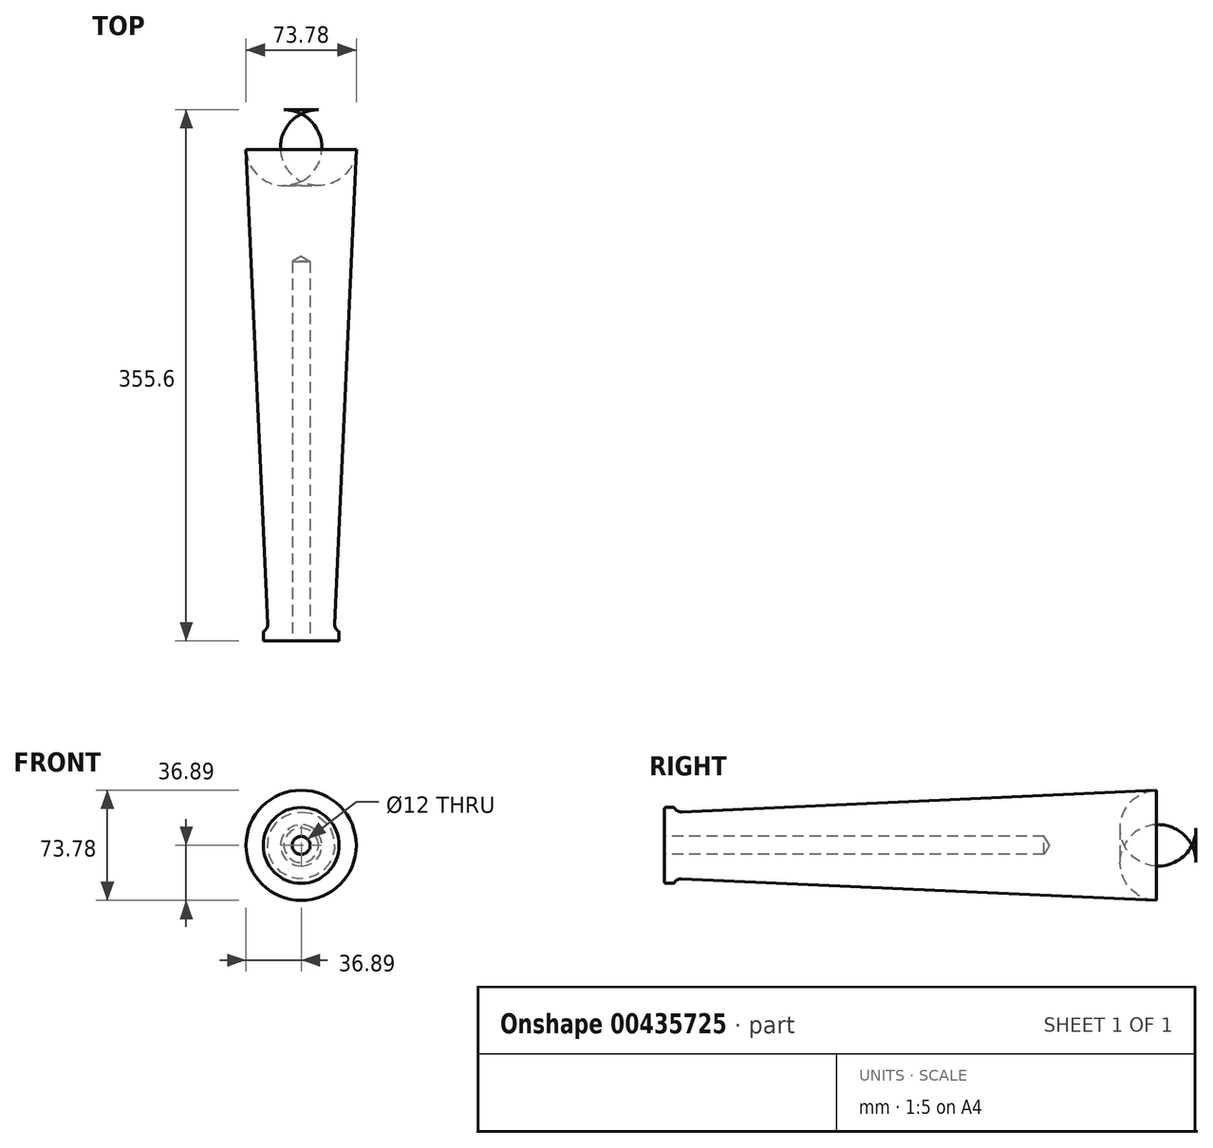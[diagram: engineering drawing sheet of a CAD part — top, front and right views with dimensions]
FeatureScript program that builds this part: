
annotation { "Feature Type Name" : "Feature", "Feature Type Description" : "" }
export const myFeature = defineFeature(function(context is Context, id is Id, definition is map)
    precondition{}
    {
        {
            var Q0;
            Q0=qCreatedBy(makeId("Right.planeOp"),FACE);
            var sketch = newSketch(context, id + "F0", { "sketchPlane" : qUnion([Q0])});
            skLineSegment(sketch, "E0", {"start": v(-254, 25.4) * mm, "end": v(-247.65, 25.4) * mm});
            skLineSegment(sketch, "E1", {"start": v(-247.65, 25.4) * mm, "end": v(-247.65, 22.22) * mm});
            skLineSegment(sketch, "E2", {"start": v(-247.65, 22.22) * mm, "end": v(101.6, 38.1) * mm});
            skLineSegment(sketch, "E3", {"start": v(101.6, 38.1) * mm, "end": v(101.6, 0) * mm});
            skLineSegment(sketch, "E4", {"start": v(-254, 25.4) * mm, "end": v(-254, 0) * mm});
            skLineSegment(sketch, "E5", {"start": v(-254, 0) * mm, "end": v(101.6, 0) * mm});
            skSolve(sketch);
        }
        {
            var Q0;
            Q0=makeQuery(id+"F0.imprint","IMPRINT",FACE,{"disambiguationData":[TD([[makeQuery(id+"F0.imprint","IMPRINT",EDGE,{"derivedFrom":sQuery(id+"F0.wireOp",EDGE,"E0")}),-1.0]])]});
            var Q1;
            Q1=sQuery(id+"F0.wireOp",EDGE,"E5");
            revolve(context, id + "F1", {"entities" : qUnion([Q0]), "axis" : qUnion([Q1]), "revolveType" : RevolveType.FULL});
        }
        {
            var Q0;
            Q0=makeQuery(id+"F1.opRevolve","SWEPT_EDGE",EDGE,{"disambiguationData":[OSD([sQuery(id+"F0.wireOp",EDGE,"E1"),sQuery(id+"F0.wireOp",EDGE,"E2")])]});
            fillet(context, id + "F2", {"entities" : qUnion([Q0]), "radius" : 5.08 * mm, "tangentPropagation" : true, "allowEdgeOverflow" : false});
        }
        {
            var Q0;
            Q0=makeQuery(id+"F1.opRevolve","SWEPT_EDGE",EDGE,{"disambiguationData":[OSD([sQuery(id+"F0.wireOp",EDGE,"E0"),sQuery(id+"F0.wireOp",EDGE,"E4")])]});
            fillet(context, id + "F3", {"entities" : qUnion([Q0]), "radius" : 0.76 * mm, "tangentPropagation" : true, "allowEdgeOverflow" : false});
        }
        {
            var Q0;
            Q0=makeQuery(id+"F2.opFillet","BLEND_EDGE",EDGE,{"blendedFrom":[makeQuery(id+"F1.opRevolve","SWEPT_EDGE",EDGE,{"disambiguationData":[OSD([sQuery(id+"F0.wireOp",EDGE,"E1"),sQuery(id+"F0.wireOp",EDGE,"E2")])]}),makeQuery(id+"F1.opRevolve","SWEPT_FACE",FACE,{"disambiguationData":[OSD([sQuery(id+"F0.wireOp",EDGE,"E0")])]})],"blendedInto":[makeQuery(id+"F1.opRevolve","SWEPT_FACE",FACE,{"disambiguationData":[OSD([sQuery(id+"F0.wireOp",EDGE,"E0")])]})]});
            fillet(context, id + "F4", {"entities" : qUnion([Q0]), "radius" : 0.76 * mm, "tangentPropagation" : true, "allowEdgeOverflow" : false});
        }
        {
            var Q0;
            Q0=makeQuery(id+"F1.opRevolve","SWEPT_EDGE",EDGE,{"disambiguationData":[OSD([sQuery(id+"F0.wireOp",EDGE,"E2"),sQuery(id+"F0.wireOp",EDGE,"E3")])]});
            fillet(context, id + "F5", {"entities" : qUnion([Q0]), "radius" : 25.4 * mm, "tangentPropagation" : true, "allowEdgeOverflow" : false});
        }
        {
            var Q0;
            Q0=makeQuery(id+"F1.opRevolve","SWEPT_FACE",FACE,{"disambiguationData":[OSD([sQuery(id+"F0.wireOp",EDGE,"E4")])]});
            cPlane(context, id + "F6", {"entities" : qUnion([Q0]), "cplaneType" : CPlaneType.OFFSET, "offset" : 0 * mm, "width" : 152.4 * mm, "height" : 152.4 * mm});
        }
        {
            var Q0;
            Q0=qCreatedBy(id+"F6.planeOp",FACE);
            var sketch = newSketch(context, id + "F7", { "sketchPlane" : qUnion([Q0])});
            skCircle(sketch, "E6", {"center": v(0, 0) * mm, "radius": 11.32 * mm});
            skSolve(sketch);
        }
        {
            var Q0;
            Q0=sQuery(id+"F7.wireOp",VERTEX,"E6.center");
            var Q1;
            Q1=makeQuery(id+"F1.opRevolve","SWEPT_BODY",BODY,{"disambiguationData":[OSD([sQuery(id+"F0.wireOp",EDGE,"E0"),sQuery(id+"F0.wireOp",EDGE,"E1"),sQuery(id+"F0.wireOp",EDGE,"E2"),sQuery(id+"F0.wireOp",EDGE,"E3"),sQuery(id+"F0.wireOp",EDGE,"E4"),sQuery(id+"F0.wireOp",EDGE,"E5")])]});
            hole(context, id + "F8", {"style" : HoleStyle.SIMPLE, "endStyle" : HoleEndStyle.BLIND, "standardTappedOrClearance" : lookupTablePath({ "standard" : "ISO", "size" : "12", "type" : "Drilled" }), "standardBlindInLast" : lookupTablePath({ "standard" : "ISO", "size" : "12", "type" : "Drilled" }), "holeDiameter" : 12 * mm, "holeDepth" : 254 * mm, "isTappedThrough" : true, "tappedDepth" : 12.7 * mm, "tapClearance" : 3, "locations" : qUnion([Q0]), "scope" : qUnion([Q1])});
        }
    });
